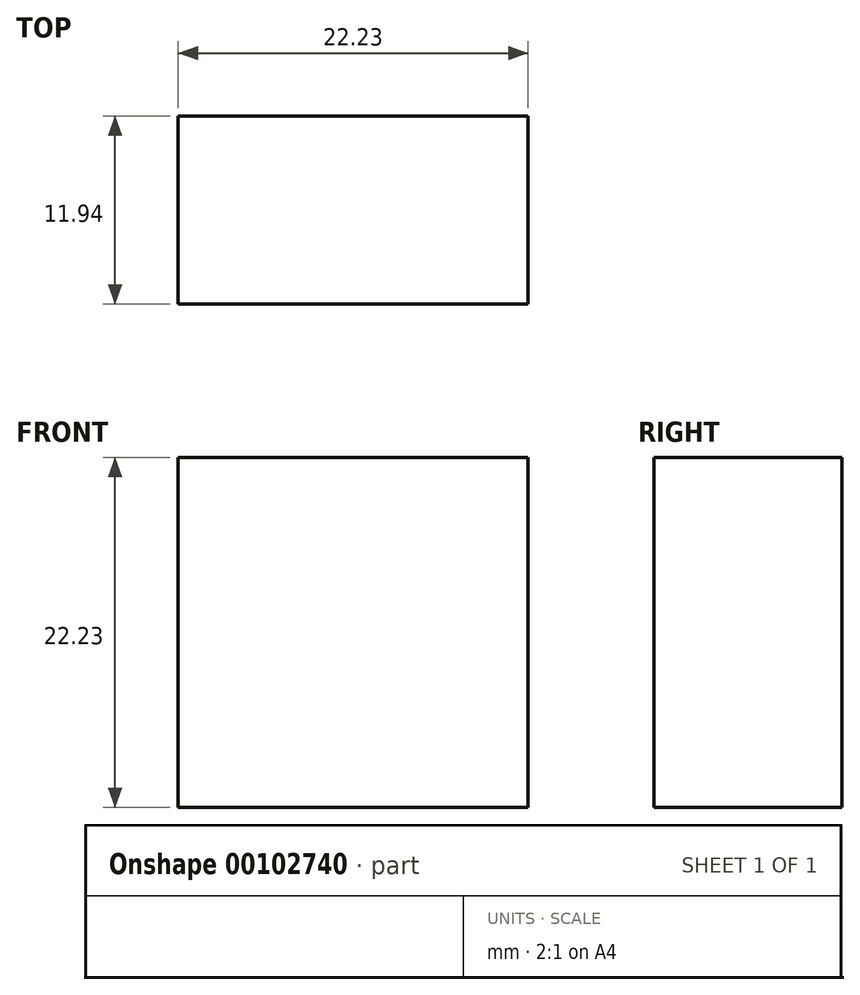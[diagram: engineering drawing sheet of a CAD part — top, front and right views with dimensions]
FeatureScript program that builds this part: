
annotation { "Feature Type Name" : "Feature", "Feature Type Description" : "" }
export const myFeature = defineFeature(function(context is Context, id is Id, definition is map)
    precondition{}
    {
        {
            var Q0;
            Q0=qCreatedBy(makeId("Front.planeOp"),FACE);
            var sketch = newSketch(context, id + "F0", { "sketchPlane" : qUnion([Q0])});
            skLineSegment(sketch, "E0.bottom", {"start": v(119.9, -109.38) * mm, "end": v(142.12, -109.38) * mm});
            skLineSegment(sketch, "E0.top", {"start": v(119.9, -131.6) * mm, "end": v(142.12, -131.6) * mm});
            skLineSegment(sketch, "E0.left", {"start": v(119.9, -109.38) * mm, "end": v(119.9, -131.6) * mm});
            skLineSegment(sketch, "E0.right", {"start": v(142.12, -109.38) * mm, "end": v(142.12, -131.6) * mm});
            skSolve(sketch);
        }
        {
            var Q0;
            Q0=makeQuery(id+"F0.imprint","IMPRINT",FACE,{"disambiguationData":[TD([[makeQuery(id+"F0.imprint","IMPRINT",EDGE,{"derivedFrom":sQuery(id+"F0.wireOp",EDGE,"E0.bottom")}),-1.0]])]});
            extrude(context, id + "F1", {"entities" : qUnion([Q0]), "depth" : 11.94 * mm});
        }
    });
